# Revit family: 11Landscaping_Bike-Racks-Shelters_Saris-Infrastructure_Tip-Up-Rack
name_source: partatom
category: Site
units: mm (PartAtom-declared; Revit-internal decimal feet)

## family parameters
Cut with Voids When Loaded = No
Host = Face
OmniClass Number = 23.40.10.11.11
Part Type = Normal
Round Connector Dimension = Use Diameter
Shared = No

## types (1)
- Tip Up Rack, Powder Coat - Black
    Date Updated = 2025/03/14
    Default Elevation = 48.00"
    Description = Tip-Up Rack, Powder Coat w/ e-coat - 6008
    Height = 32.37"
    Length = 17.25"
    Manufacturer = Saris Infrastructure
    Model = 6008
    Product Documentation Link = https://cdn.shopify.com
    Product Material = Saris Infrastructure - Mild Steel - Powder Coat - Black with e-coat
    Product Page URL = https://sarisinfrastructure.com
    Product Specifications = • Pneumatic spring powered lifting arm allows easy loading
 of bikes into the vertical position
 • Instruction decal provides clear use direction to new users
 • Locking loop provides means of securing bike using
 standard locks and prevents bike lowering when in use
 • Vertical configuration allows smaller storage footprint
 compared to horizontally oriented racks
    Product data url = https://bimobject.com
    URL = https://www.sarisinfrastructure.com
    Version = 1
    Warranty = 1 year
    Weight = 0.00 lbf
    Width = 6.00"

## geometry (parser evidence)
native form markers: Sweep x2
no freeform markers — native parametric forms only
